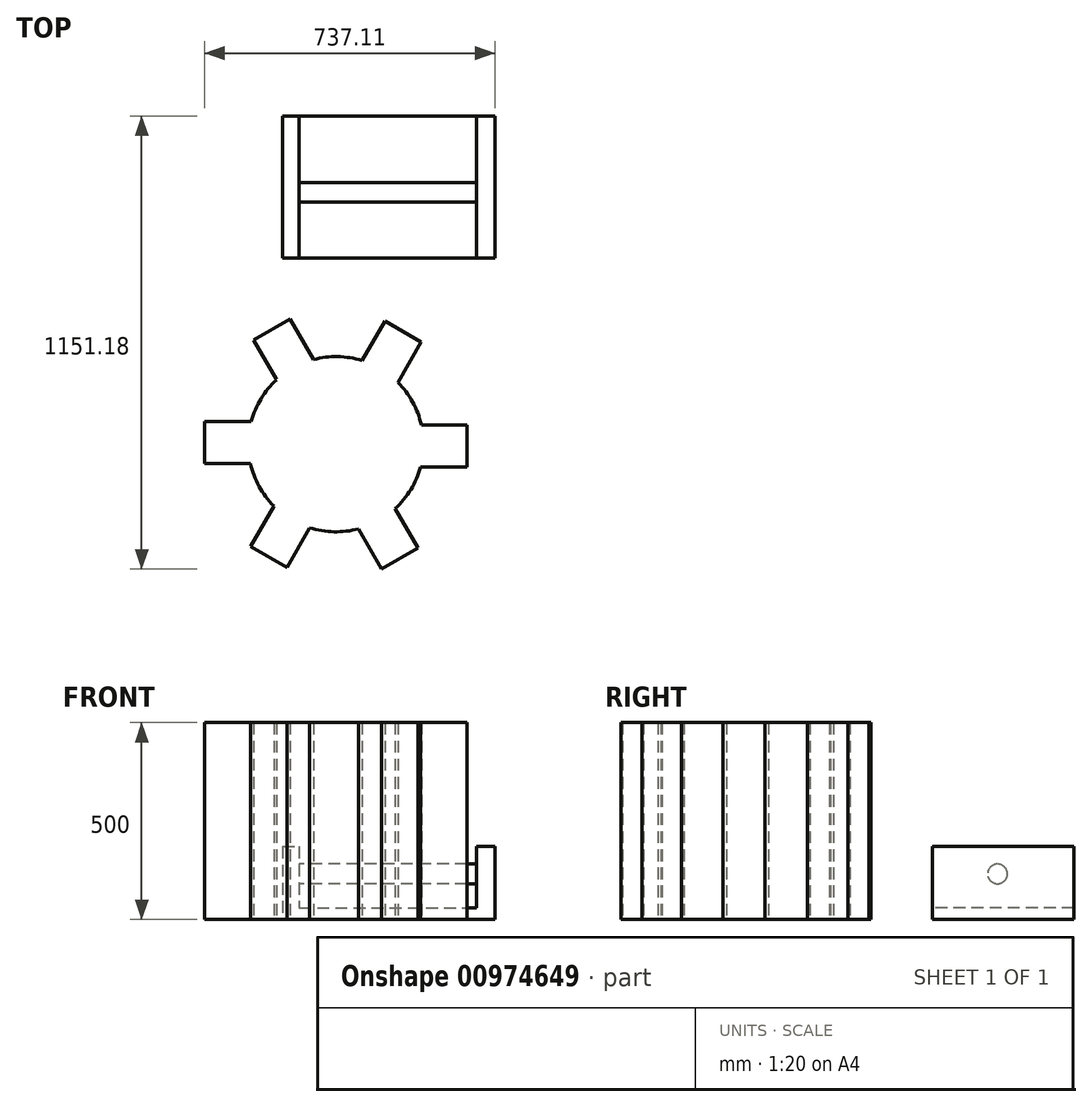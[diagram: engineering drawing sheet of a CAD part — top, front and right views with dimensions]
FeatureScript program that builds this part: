
annotation { "Feature Type Name" : "Feature", "Feature Type Description" : "" }
export const myFeature = defineFeature(function(context is Context, id is Id, definition is map)
    precondition{}
    {
        {
            var Q0;
            Q0=qCreatedBy(makeId("Top.planeOp"),FACE);
            var sketch = newSketch(context, id + "F0", { "sketchPlane" : qUnion([Q0])});
            skCircle(sketch, "E0", {"center": v(0, 0) * mm, "radius": 222.55 * mm});
            skLineSegment(sketch, "E1.bottom", {"start": v(182.58, -57.9) * mm, "end": v(333.18, -57.9) * mm});
            skLineSegment(sketch, "E1.top", {"start": v(182.58, 48.77) * mm, "end": v(333.18, 48.77) * mm});
            skLineSegment(sketch, "E1.left", {"start": v(182.58, -57.9) * mm, "end": v(182.58, 48.77) * mm});
            skLineSegment(sketch, "E1.right", {"start": v(333.18, -57.9) * mm, "end": v(333.18, 48.77) * mm});
            skLineSegment(sketch, "E2.1.0", {"start": v(141.43, 129.17) * mm, "end": v(216.73, 259.6) * mm});
            skLineSegment(sketch, "E2.1.1", {"start": v(141.43, 129.17) * mm, "end": v(49.05, 182.5) * mm});
            skLineSegment(sketch, "E2.1.2", {"start": v(49.05, 182.5) * mm, "end": v(124.35, 312.93) * mm});
            skLineSegment(sketch, "E2.1.3", {"start": v(216.73, 259.6) * mm, "end": v(124.35, 312.93) * mm});
            skLineSegment(sketch, "E2.2.0", {"start": v(-41.15, 187.07) * mm, "end": v(-116.45, 317.5) * mm});
            skLineSegment(sketch, "E2.2.1", {"start": v(-41.15, 187.07) * mm, "end": v(-133.53, 133.73) * mm});
            skLineSegment(sketch, "E2.2.2", {"start": v(-133.53, 133.73) * mm, "end": v(-208.83, 264.16) * mm});
            skLineSegment(sketch, "E2.2.3", {"start": v(-116.45, 317.5) * mm, "end": v(-208.83, 264.16) * mm});
            skLineSegment(sketch, "E2.3.0", {"start": v(-182.58, 57.9) * mm, "end": v(-333.18, 57.9) * mm});
            skLineSegment(sketch, "E2.3.1", {"start": v(-182.58, 57.9) * mm, "end": v(-182.58, -48.77) * mm});
            skLineSegment(sketch, "E2.3.2", {"start": v(-182.58, -48.77) * mm, "end": v(-333.18, -48.77) * mm});
            skLineSegment(sketch, "E2.3.3", {"start": v(-333.18, 57.9) * mm, "end": v(-333.18, -48.77) * mm});
            skLineSegment(sketch, "E2.4.0", {"start": v(-141.43, -129.17) * mm, "end": v(-216.73, -259.6) * mm});
            skLineSegment(sketch, "E2.4.1", {"start": v(-141.43, -129.17) * mm, "end": v(-49.05, -182.5) * mm});
            skLineSegment(sketch, "E2.4.2", {"start": v(-49.05, -182.5) * mm, "end": v(-124.35, -312.93) * mm});
            skLineSegment(sketch, "E2.4.3", {"start": v(-216.73, -259.6) * mm, "end": v(-124.35, -312.93) * mm});
            skLineSegment(sketch, "E2.5.0", {"start": v(41.15, -187.07) * mm, "end": v(116.45, -317.5) * mm});
            skLineSegment(sketch, "E2.5.1", {"start": v(41.15, -187.07) * mm, "end": v(133.53, -133.73) * mm});
            skLineSegment(sketch, "E2.5.2", {"start": v(133.53, -133.73) * mm, "end": v(208.83, -264.16) * mm});
            skLineSegment(sketch, "E2.5.3", {"start": v(116.45, -317.5) * mm, "end": v(208.83, -264.16) * mm});
            skSolve(sketch);
        }
        {
            var Q0;
            Q0 = qSketchRegion(id + "F0", true);
            extrude(context, id + "F1", {"entities" : qUnion([Q0]), "depth" : 500 * mm, "offsetDistance" : 25 * mm});
        }
        {
            var Q0;
            Q0=qCreatedBy(makeId("Top.planeOp"),FACE);
            var sketch = newSketch(context, id + "F2", { "sketchPlane" : qUnion([Q0])});
            skLineSegment(sketch, "E3.bottom", {"start": v(-134.89, 473.52) * mm, "end": v(403.93, 473.52) * mm});
            skLineSegment(sketch, "E3.top", {"start": v(-134.89, 833.69) * mm, "end": v(403.93, 833.69) * mm});
            skLineSegment(sketch, "E3.left", {"start": v(-134.89, 473.52) * mm, "end": v(-134.89, 833.69) * mm});
            skLineSegment(sketch, "E3.right", {"start": v(403.93, 473.52) * mm, "end": v(403.93, 833.69) * mm});
            skSolve(sketch);
        }
        {
            var Q0;
            Q0=makeQuery(id+"F2.imprint","IMPRINT",FACE,{"disambiguationData":[TD([[makeQuery(id+"F2.imprint","IMPRINT",EDGE,{"derivedFrom":sQuery(id+"F2.wireOp",EDGE,"E3.bottom")}),1.0]])]});
            extrude(context, id + "F3", {"entities" : qUnion([Q0]), "depth" : 30 * mm, "offsetDistance" : 25 * mm});
        }
        {
            var Q0;
            Q0=makeQuery(id+"F3.opExtrude","CAP_FACE",FACE,{"disambiguationData":[OSD([sQuery(id+"F2.wireOp",EDGE,"E3.bottom"),sQuery(id+"F2.wireOp",EDGE,"E3.top"),sQuery(id+"F2.wireOp",EDGE,"E3.left"),sQuery(id+"F2.wireOp",EDGE,"E3.right")])],"isStart":false});
            var sketch = newSketch(context, id + "F4", { "sketchPlane" : qUnion([Q0])});
            skLineSegment(sketch, "E4.bottom", {"start": v(-134.89, 473.52) * mm, "end": v(-93.05, 473.52) * mm});
            skLineSegment(sketch, "E4.top", {"start": v(-134.89, 833.69) * mm, "end": v(-93.05, 833.69) * mm});
            skLineSegment(sketch, "E4.left", {"start": v(-134.89, 473.52) * mm, "end": v(-134.89, 833.69) * mm});
            skLineSegment(sketch, "E4.right", {"start": v(-93.05, 473.52) * mm, "end": v(-93.05, 833.69) * mm});
            skSolve(sketch);
        }
        {
            var Q0;
            Q0=makeQuery(id+"F4.imprint","IMPRINT",FACE,{"disambiguationData":[TD([[makeQuery(id+"F4.imprint","IMPRINT",EDGE,{"derivedFrom":sQuery(id+"F4.wireOp",EDGE,"E4.bottom")}),1.0]])]});
            extrude(context, id + "F5", {"entities" : qUnion([Q0]), "operationType" : NewBodyOperationType.ADD, "depth" : 155 * mm, "offsetDistance" : 25 * mm});
        }
        {
            var Q0;
            Q0=makeQuery(id+"F5.opExtrude","SWEPT_FACE",FACE,{"disambiguationData":[OSD([sQuery(id+"F4.wireOp",EDGE,"E4.right")])]});
            var sketch = newSketch(context, id + "F6", { "sketchPlane" : qUnion([Q0])});
            skCircle(sketch, "E5", {"center": v(639.63, 115.64) * mm, "radius": 25.04 * mm});
            skSolve(sketch);
        }
        {
            var Q0;
            Q0=makeQuery(id+"F3.opExtrude","CAP_FACE",FACE,{"disambiguationData":[OSD([sQuery(id+"F2.wireOp",EDGE,"E3.bottom"),sQuery(id+"F2.wireOp",EDGE,"E3.top"),sQuery(id+"F2.wireOp",EDGE,"E3.left"),sQuery(id+"F2.wireOp",EDGE,"E3.right")])],"isStart":false});
            var sketch = newSketch(context, id + "F7", { "sketchPlane" : qUnion([Q0])});
            skLineSegment(sketch, "E6.bottom", {"start": v(403.93, 833.69) * mm, "end": v(357.79, 833.69) * mm});
            skLineSegment(sketch, "E6.top", {"start": v(403.93, 473.52) * mm, "end": v(357.79, 473.52) * mm});
            skLineSegment(sketch, "E6.left", {"start": v(403.93, 833.69) * mm, "end": v(403.93, 473.52) * mm});
            skLineSegment(sketch, "E6.right", {"start": v(357.79, 833.69) * mm, "end": v(357.79, 473.52) * mm});
            skSolve(sketch);
        }
        {
            var Q0;
            Q0=makeQuery(id+"F7.imprint","IMPRINT",FACE,{"disambiguationData":[TD([[makeQuery(id+"F7.imprint","IMPRINT",EDGE,{"derivedFrom":sQuery(id+"F7.wireOp",EDGE,"E6.bottom")}),-1.0]])]});
            extrude(context, id + "F8", {"entities" : qUnion([Q0]), "operationType" : NewBodyOperationType.ADD, "depth" : 155 * mm, "offsetDistance" : 25 * mm});
        }
        {
            var Q0;
            Q0=makeQuery(id+"F6.imprint","IMPRINT",FACE,{"disambiguationData":[TD([[makeQuery(id+"F6.imprint","IMPRINT",EDGE,{"derivedFrom":sQuery(id+"F6.wireOp",EDGE,"E5")}),1.0]])]});
            var Q1;
            Q1=sQuery(id+"F6.wireOp",EDGE,"E5");
            extrude(context, id + "F9", {"entities" : qUnion([Q0]), "operationType" : NewBodyOperationType.ADD, "surfaceOperationType" : NewSurfaceOperationType.ADD, "surfaceEntities" : qUnion([Q1]), "endBound" : BoundingType.UP_TO_NEXT, "depth" : 25 * mm, "offsetDistance" : 25 * mm});
        }
    });
